# Revit family: Bathtub-Apron-DXV-HAWKINS-D1246X002.415_Series
name_source: partatom
category: Plumbing Fixtures
revit_build: Autodesk Revit 2014 (Build: 20130308_1515(x64)
units: mm (PartAtom-declared; Revit-internal decimal feet)

## types (2) — shared parameters
Assembly Code = D2010510
Body Material = Americast-DXV-415-Canvas White
CW Connection = No
CWFU = 3
Default Elevation = 0"
HW Connection = No
HWFU = 3
Height = 17 3/8"
Installation Type = Floor Mounted
Length = 60"
Manufacturer = DXV
Material = Americast-DXV-415-Canvas White
Price = Prices may vary. Please consult Manufacturer Representative for most up-to-date price list.
Product Documentation Link = https://dxv01.blob.core.windows.net
Product Page URL = https://www.dxv.com
URL = http://www.dxv.com
Vent Connection = No
WFU = 4
Warranty Documentation Link = https://www.dxv.com
Waste Connection = Yes
Waste Connection Diameter = 1 1/2"
Waste Connection Radius = 3/4"
Waste Connection Width = 8"
Width = 32"

## per-type parameters (varying)
| type | Bath Tub | Description | Drain Location |
| D12461002 | Bathtub-ALCOVE-DXV-HAWKINS-D12461002 : D12461002.415 | HAWKINS ALCOVE TUB  Right-Hand Outlet | 15 5/8" |
| D12460002 | Bathtub-ALCOVE-DXV-HAWKINS-D12460002 : D12460002.415 | HAWKINS ALCOVE TUB  Left-Hand Outlet | 59 5/8" |

note: column(s) folded — value = type name in every type: Model

## geometry (parser evidence)
native form markers: Sweep x9
no freeform markers — native parametric forms only
